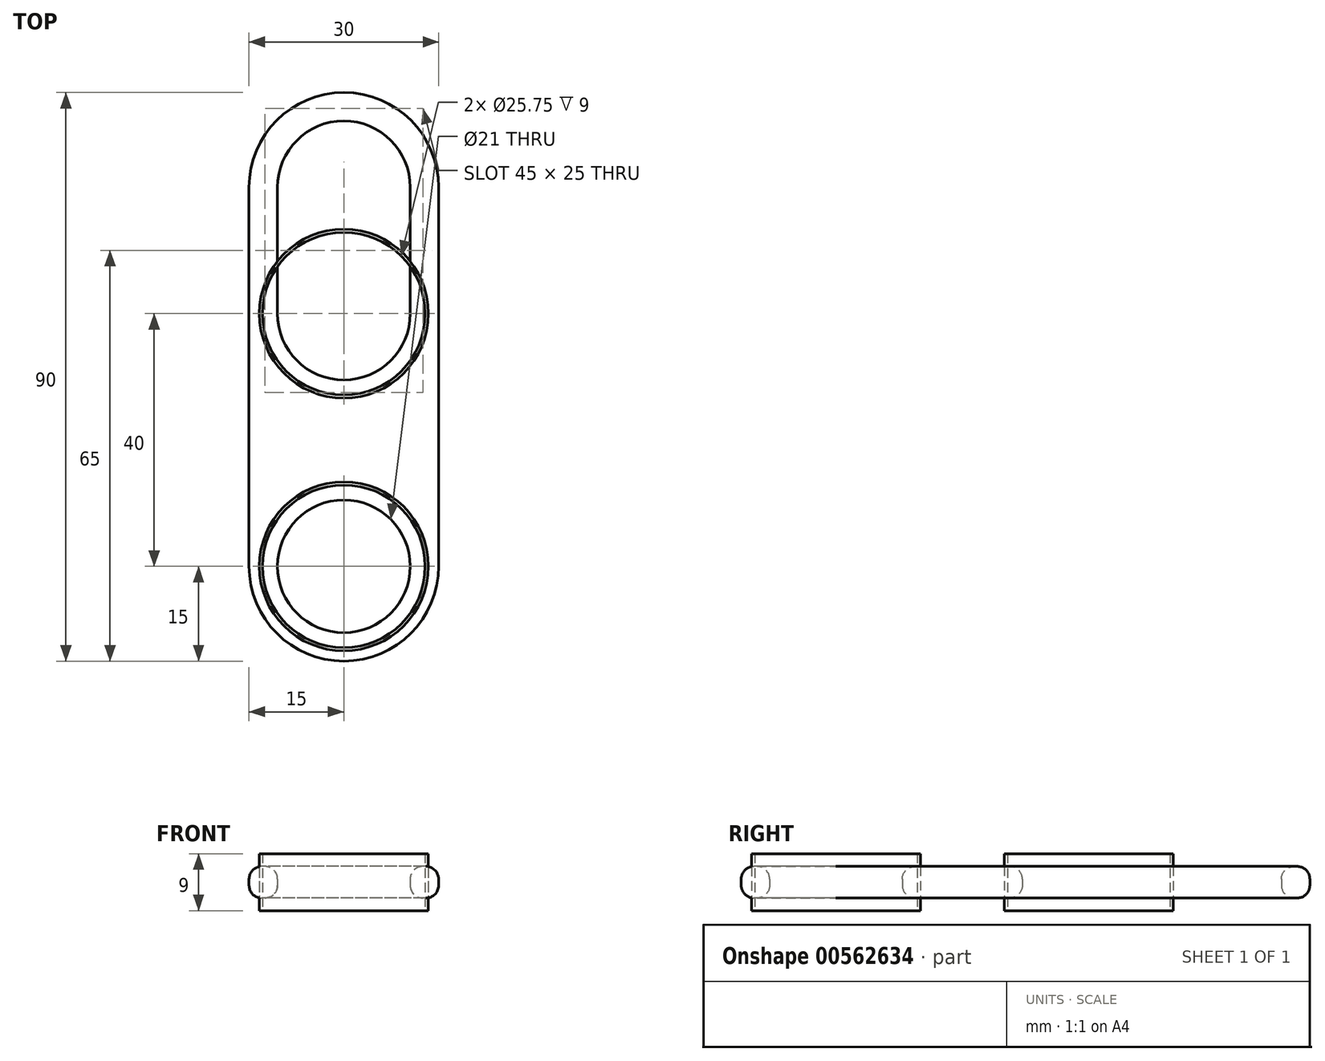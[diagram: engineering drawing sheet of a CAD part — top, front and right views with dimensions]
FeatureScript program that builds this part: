
annotation { "Feature Type Name" : "Feature", "Feature Type Description" : "" }
export const myFeature = defineFeature(function(context is Context, id is Id, definition is map)
    precondition{}
    {
        {
            var Q0;
            Q0=qCreatedBy(makeId("Top.planeOp"),FACE);
            var sketch = newSketch(context, id + "F0", { "sketchPlane" : qUnion([Q0])});
            skLineSegment(sketch, "E0", {"start": v(0, 30) * mm, "end": v(0, -30) * mm});
            skArc(sketch, "E1.0.startCap", {"start": v(-15, 30) * mm, "mid": v(0, 45) * mm, "end": v(15, 30) * mm});
            skArc(sketch, "E1.0.endCap", {"start": v(15, -30) * mm, "mid": v(0, -45) * mm, "end": v(-15, -30) * mm});
            skLineSegment(sketch, "E1.0.left", {"start": v(15, 30) * mm, "end": v(15, -30) * mm});
            skLineSegment(sketch, "E1.0.right", {"start": v(-15, 30) * mm, "end": v(-15, -30) * mm});
            skArc(sketch, "E2", {"start": v(10.5, 30) * mm, "mid": v(0, 40.5) * mm, "end": v(-10.5, 30) * mm});
            skPoint(sketch, "E3.center", {"position": v(0, -0.5) * mm});
            skArc(sketch, "E4", {"start": v(-10.5, 10) * mm, "mid": v(0, -0.5) * mm, "end": v(10.5, 10) * mm});
            skLineSegment(sketch, "E5", {"start": v(10.5, 30) * mm, "end": v(10.5, 10) * mm});
            skLineSegment(sketch, "E6", {"start": v(-10.5, 30) * mm, "end": v(-10.5, 10) * mm});
            skPoint(sketch, "E7.orphan", {"position": v(-12.33, 0) * mm});
            skPoint(sketch, "E8.end.orphan", {"position": v(15, 0) * mm});
            skCircle(sketch, "E9", {"center": v(0, -30) * mm, "radius": 10.5 * mm});
            skSolve(sketch);
        }
        {
            var Q0;
            Q0=qSketchRegion(id+"F0",true);
            extrude(context, id + "F1", {"entities" : qUnion([Q0]), "depth" : 5 * mm, "offsetDistance" : 25 * mm});
        }
        {
            var Q0;
            Q0=makeQuery(id+"F1.opExtrude","CAP_EDGE",EDGE,{"disambiguationData":[OSD([sQuery(id+"F0.wireOp",EDGE,"E2")])],"isStart":false});
            var Q1;
            Q1=makeQuery(id+"F1.opExtrude","CAP_EDGE",EDGE,{"disambiguationData":[OSD([sQuery(id+"F0.wireOp",EDGE,"E2")])],"isStart":true});
            var Q2;
            Q2=makeQuery(id+"F1.opExtrude","CAP_EDGE",EDGE,{"disambiguationData":[OSD([sQuery(id+"F0.wireOp",EDGE,"E1.0.left")])],"isStart":true});
            var Q3;
            Q3=makeQuery(id+"F1.opExtrude","CAP_EDGE",EDGE,{"disambiguationData":[OSD([sQuery(id+"F0.wireOp",EDGE,"E9")])],"isStart":false});
            var Q4;
            Q4=makeQuery(id+"F1.opExtrude","CAP_EDGE",EDGE,{"disambiguationData":[OSD([sQuery(id+"F0.wireOp",EDGE,"E9")])],"isStart":true});
            fillet(context, id + "F2", {"entities" : qUnion([Q0, Q1, Q2, Q3, Q4]), "radius" : 2 * mm, "tangentPropagation" : true, "allowEdgeOverflow" : false});
        }
        {
            var Q0;
            Q0=makeQuery(id+"F1.opExtrude","CAP_EDGE",EDGE,{"disambiguationData":[OSD([sQuery(id+"F0.wireOp",EDGE,"E1.0.right")])],"isStart":false});
            fillet(context, id + "F3", {"entities" : qUnion([Q0]), "radius" : 2 * mm, "tangentPropagation" : true, "allowEdgeOverflow" : false});
        }
        {
            var Q0;
            Q0=qCreatedBy(makeId("Top.planeOp"),FACE);
            var sketch = newSketch(context, id + "F4", { "sketchPlane" : qUnion([Q0])});
            skCircle(sketch, "E10", {"center": v(0, -30) * mm, "radius": 12.88 * mm});
            skCircle(sketch, "E11", {"center": v(0, -30) * mm, "radius": 13.38 * mm});
            skSolve(sketch);
        }
        {
            var Q0;
            Q0 = qSketchRegion(id + "F4", true);
            extrude(context, id + "F5", {"entities" : qUnion([Q0]), "depth" : 7 * mm, "offsetDistance" : 25 * mm, "hasSecondDirection" : true, "secondDirectionOppositeDirection" : true, "secondDirectionDepth" : 2 * mm});
        }
        {
            var Q0;
            Q0=qCreatedBy(makeId("Top.planeOp"),FACE);
            var sketch = newSketch(context, id + "F6", { "sketchPlane" : qUnion([Q0])});
            skCircle(sketch, "E12", {"center": v(0, 10) * mm, "radius": 12.88 * mm});
            skCircle(sketch, "E13", {"center": v(0, 10) * mm, "radius": 13.38 * mm});
            skSolve(sketch);
        }
        {
            var Q0;
            Q0 = qSketchRegion(id + "F6", true);
            extrude(context, id + "F7", {"entities" : qUnion([Q0]), "depth" : 7 * mm, "offsetDistance" : 25 * mm, "hasSecondDirection" : true, "secondDirectionOppositeDirection" : true, "secondDirectionDepth" : 2 * mm});
        }
    });
